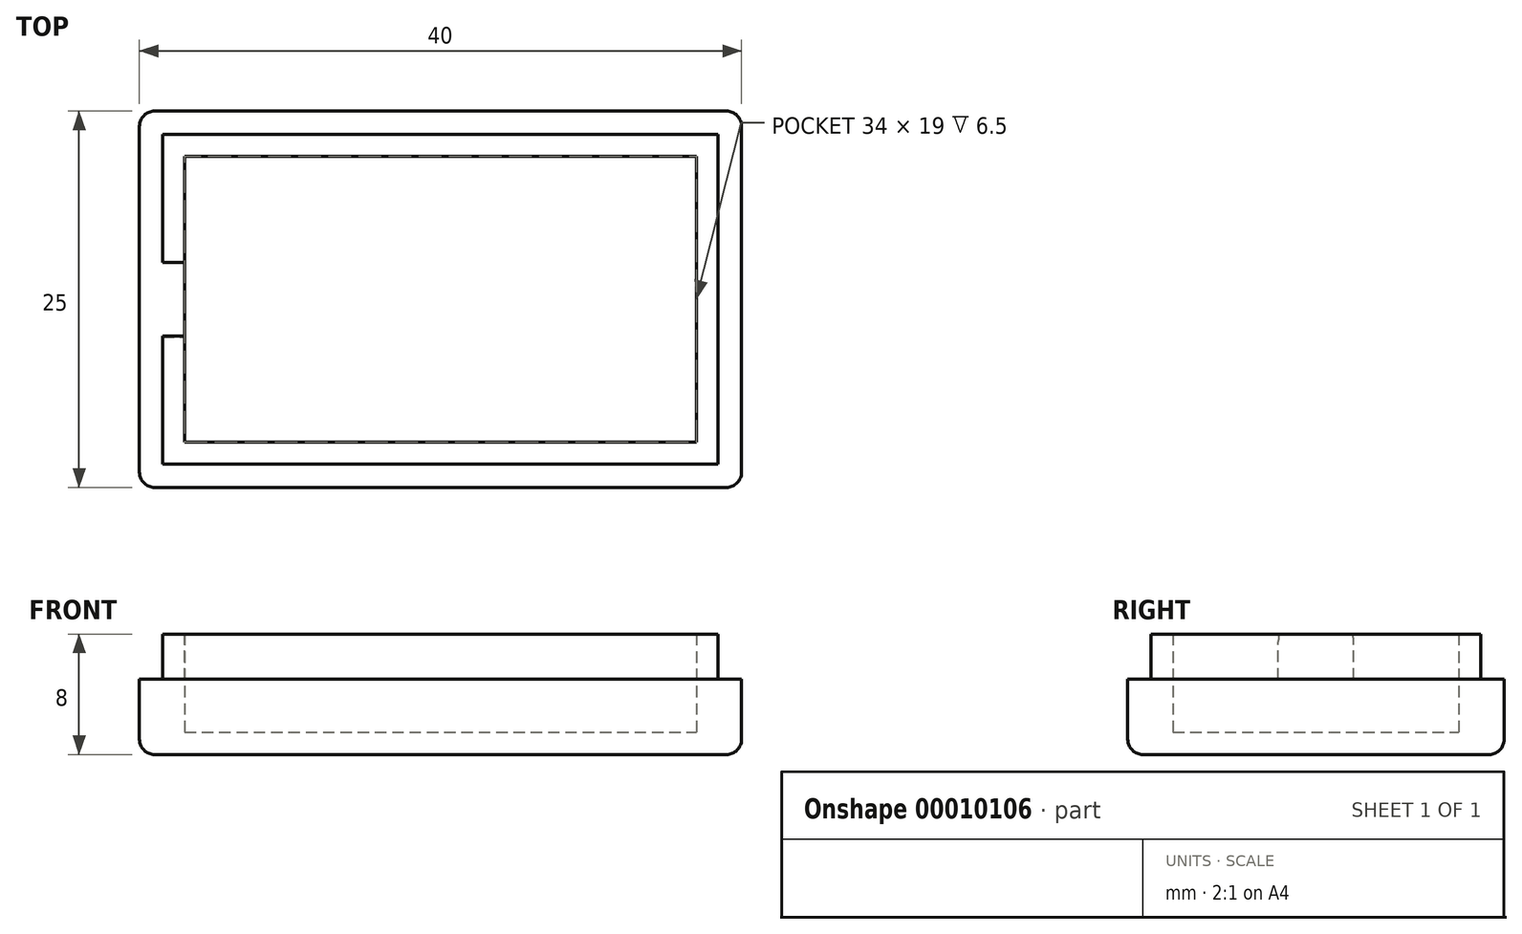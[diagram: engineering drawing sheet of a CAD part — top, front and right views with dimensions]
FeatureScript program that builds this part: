
annotation { "Feature Type Name" : "Feature", "Feature Type Description" : "" }
export const myFeature = defineFeature(function(context is Context, id is Id, definition is map)
    precondition{}
    {
        {
            var Q0;
            Q0=qCreatedBy(makeId("Top.planeOp"),FACE);
            var sketch = newSketch(context, id + "F0", { "sketchPlane" : qUnion([Q0])});
            skLineSegment(sketch, "E0.rect.bottom", {"start": v(20, 12.5) * mm, "end": v(-20, 12.5) * mm});
            skLineSegment(sketch, "E0.rect.top", {"start": v(20, -12.5) * mm, "end": v(-20, -12.5) * mm});
            skLineSegment(sketch, "E0.rect.left", {"start": v(20, 12.5) * mm, "end": v(20, -12.5) * mm});
            skLineSegment(sketch, "E0.rect.right", {"start": v(-20, 12.5) * mm, "end": v(-20, -12.5) * mm});
            skPoint(sketch, "E0.rect.middle", {"position": v(0, 0) * mm});
            skLineSegment(sketch, "E1.rect.bottom", {"start": v(17, 9.5) * mm, "end": v(-17, 9.5) * mm});
            skLineSegment(sketch, "E1.rect.top", {"start": v(17, -9.5) * mm, "end": v(-17, -9.5) * mm});
            skLineSegment(sketch, "E1.rect.left", {"start": v(17, 9.5) * mm, "end": v(17, -9.5) * mm});
            skLineSegment(sketch, "E1.rect.right", {"start": v(-17, 9.5) * mm, "end": v(-17, -9.5) * mm});
            skLineSegment(sketch, "E2", {"start": v(20, -3.98) * mm, "end": v(17, -3.98) * mm, "construction": true});
            skLineSegment(sketch, "E3", {"start": v(16.8, 12.5) * mm, "end": v(16.8, 9.5) * mm, "construction": true});
            skLineSegment(sketch, "E4.rect.bottom", {"start": v(18.45, 10.95) * mm, "end": v(-18.45, 10.95) * mm});
            skLineSegment(sketch, "E4.rect.top", {"start": v(18.45, -10.95) * mm, "end": v(-18.45, -10.95) * mm});
            skLineSegment(sketch, "E4.rect.left", {"start": v(18.45, 10.95) * mm, "end": v(18.45, -10.95) * mm});
            skLineSegment(sketch, "E4.rect.right", {"start": v(-18.45, 10.95) * mm, "end": v(-18.45, -10.95) * mm});
            skLineSegment(sketch, "E5", {"start": v(-17, 7.8) * mm, "end": v(-18.45, 7.8) * mm, "construction": true});
            skLineSegment(sketch, "E6", {"start": v(-10.2, 9.5) * mm, "end": v(-10.2, 10.95) * mm, "construction": true});
            skSolve(sketch);
        }
        {
            var Q0;
            Q0=makeQuery(id+"F0.imprint","IMPRINT",FACE,{"disambiguationData":[TD([[makeQuery(id+"F0.imprint","IMPRINT",EDGE,{"derivedFrom":sQuery(id+"F0.wireOp",EDGE,"E0.rect.bottom")}),1.0]])]});
            extrude(context, id + "F1", {"entities" : qUnion([Q0]), "depth" : 5 * mm});
        }
        {
            var Q0;
            Q0=makeQuery(id+"F1.opExtrude","CAP_EDGE",EDGE,{"disambiguationData":[OSD([sQuery(id+"F0.wireOp",EDGE,"E0.rect.right")])],"isStart":true});
            var Q1;
            Q1=makeQuery(id+"F1.opExtrude","CAP_EDGE",EDGE,{"disambiguationData":[OSD([sQuery(id+"F0.wireOp",EDGE,"E0.rect.top")])],"isStart":true});
            var Q2;
            Q2=makeQuery(id+"F1.opExtrude","CAP_EDGE",EDGE,{"disambiguationData":[OSD([sQuery(id+"F0.wireOp",EDGE,"E0.rect.bottom")])],"isStart":true});
            var Q3;
            Q3=makeQuery(id+"F1.opExtrude","CAP_EDGE",EDGE,{"disambiguationData":[OSD([sQuery(id+"F0.wireOp",EDGE,"E0.rect.left")])],"isStart":true});
            var Q4;
            Q4=makeQuery(id+"F1.opExtrude","SWEPT_EDGE",EDGE,{"disambiguationData":[OSD([sQuery(id+"F0.wireOp",EDGE,"E0.rect.bottom"),sQuery(id+"F0.wireOp",EDGE,"E0.rect.right")])]});
            var Q5;
            Q5=makeQuery(id+"F1.opExtrude","SWEPT_EDGE",EDGE,{"disambiguationData":[OSD([sQuery(id+"F0.wireOp",EDGE,"E0.rect.bottom"),sQuery(id+"F0.wireOp",EDGE,"E0.rect.left")])]});
            var Q6;
            Q6=makeQuery(id+"F1.opExtrude","SWEPT_EDGE",EDGE,{"disambiguationData":[OSD([sQuery(id+"F0.wireOp",EDGE,"E0.rect.top"),sQuery(id+"F0.wireOp",EDGE,"E0.rect.right")])]});
            var Q7;
            Q7=makeQuery(id+"F1.opExtrude","SWEPT_EDGE",EDGE,{"disambiguationData":[OSD([sQuery(id+"F0.wireOp",EDGE,"E0.rect.top"),sQuery(id+"F0.wireOp",EDGE,"E0.rect.left")])]});
            fillet(context, id + "F2", {"entities" : qUnion([Q0, Q1, Q2, Q3, Q4, Q5, Q6, Q7]), "radius" : 1 * mm, "tangentPropagation" : true, "allowEdgeOverflow" : false});
        }
        {
            var Q0;
            Q0=makeQuery(id+"F0.imprint","IMPRINT",FACE,{"disambiguationData":[TD([[makeQuery(id+"F0.imprint","IMPRINT",EDGE,{"derivedFrom":sQuery(id+"F0.wireOp",EDGE,"E1.rect.bottom")}),1.0]])]});
            var Q1;
            Q1=makeQuery(id+"F0.imprint","IMPRINT",FACE,{"disambiguationData":[TD([[makeQuery(id+"F0.imprint","IMPRINT",EDGE,{"derivedFrom":sQuery(id+"F0.wireOp",EDGE,"E1.rect.bottom")}),-1.0]])]});
            extrude(context, id + "F3", {"entities" : qUnion([Q0, Q1]), "depth" : 1.5 * mm});
        }
        {
            var Q0;
            Q0=makeQuery(id+"F0.imprint","IMPRINT",FACE,{"disambiguationData":[TD([[makeQuery(id+"F0.imprint","IMPRINT",EDGE,{"derivedFrom":sQuery(id+"F0.wireOp",EDGE,"E1.rect.bottom")}),-1.0]])]});
            extrude(context, id + "F4", {"entities" : qUnion([Q0]), "operationType" : NewBodyOperationType.ADD, "depth" : 8 * mm});
        }
        {
            var Q0;
            Q0=qCreatedBy(makeId("Right.planeOp"),FACE);
            var sketch = newSketch(context, id + "F5", { "sketchPlane" : qUnion([Q0])});
            skLineSegment(sketch, "E7.0.MirrorCS", {"start": v(0, 5) * mm, "end": v(-2.5, 5) * mm});
            skArc(sketch, "E8.0.MirrorCS", {"start": v(-2.5, 7.5) * mm, "mid": v(-1.77, 9.27) * mm, "end": v(0, 10) * mm});
            skLineSegment(sketch, "E9.0.MirrorCS", {"start": v(-2.5, 5) * mm, "end": v(-2.5, 7.5) * mm});
            skLineSegment(sketch, "E10.0.MirrorCS", {"start": v(0, 5) * mm, "end": v(2.5, 5) * mm});
            skLineSegment(sketch, "E11.0.MirrorCS", {"start": v(2.5, 5) * mm, "end": v(2.5, 7.5) * mm});
            skArc(sketch, "E12.0.MirrorCS", {"start": v(2.5, 7.5) * mm, "mid": v(1.77, 9.27) * mm, "end": v(0, 10) * mm});
            skLineSegment(sketch, "E13", {"start": v(0, 0) * mm, "end": v(0, 5) * mm, "construction": true});
            skSolve(sketch);
        }
        {
            var Q0;
            Q0 = qSketchRegion(id + "F5", true);
            extrude(context, id + "F6", {"entities" : qUnion([Q0]), "operationType" : NewBodyOperationType.REMOVE, "oppositeDirection" : true, "depth" : 87.81 * mm});
        }
    });
